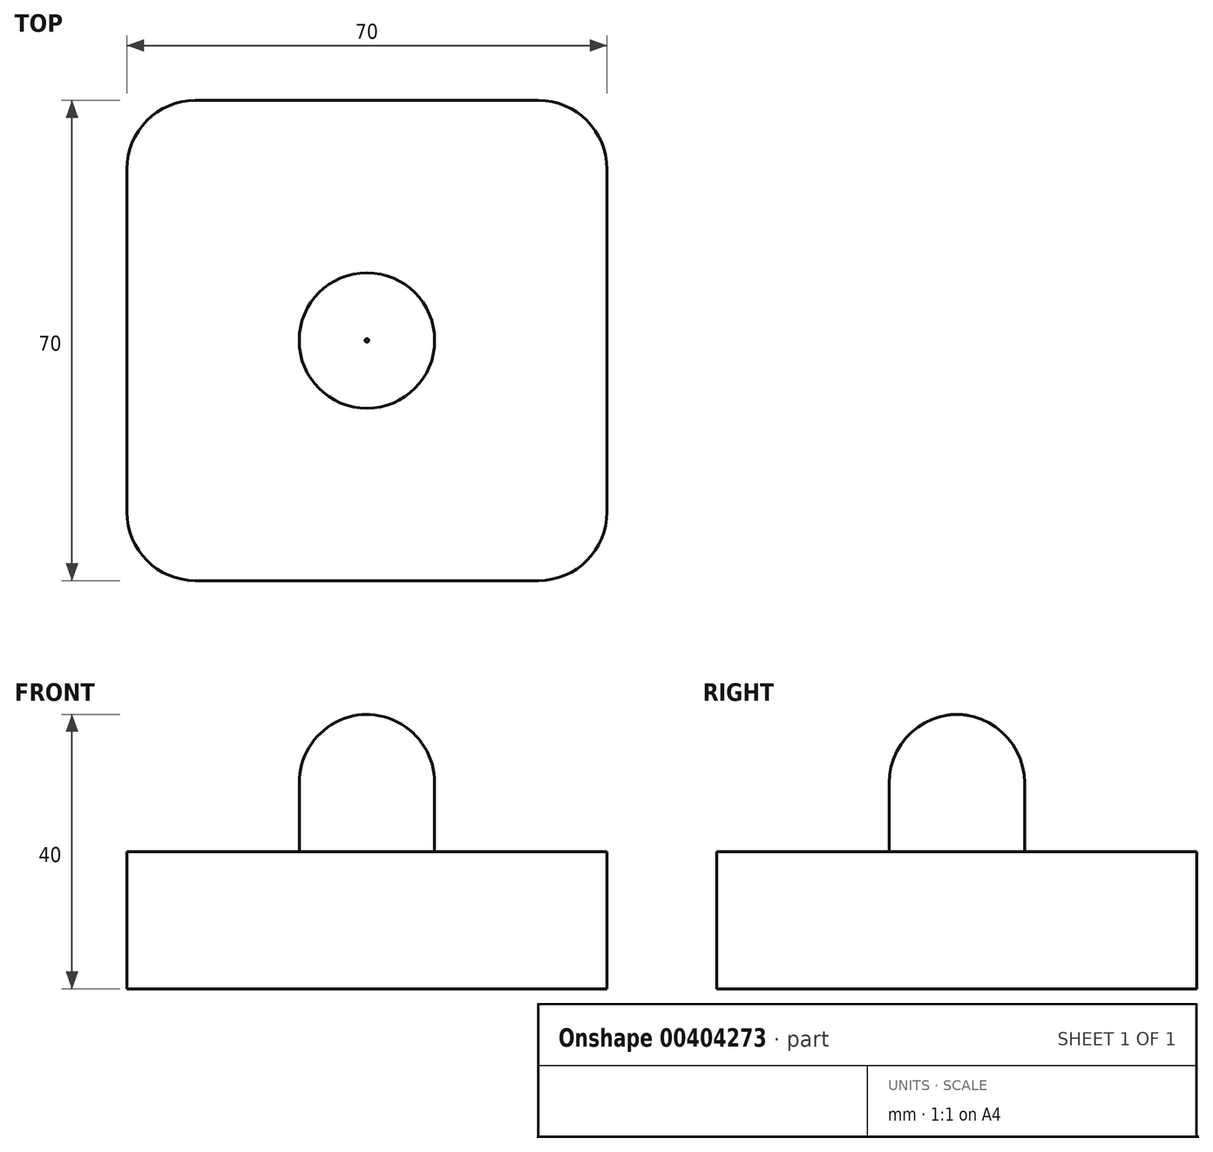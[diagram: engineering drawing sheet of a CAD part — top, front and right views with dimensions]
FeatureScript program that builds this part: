
annotation { "Feature Type Name" : "Feature", "Feature Type Description" : "" }
export const myFeature = defineFeature(function(context is Context, id is Id, definition is map)
    precondition{}
    {
        {
            var Q0;
            Q0=qCreatedBy(makeId("Top.planeOp"),FACE);
            var sketch = newSketch(context, id + "F0", { "sketchPlane" : qUnion([Q0])});
            skLineSegment(sketch, "E0.bottom", {"start": v(35, -35) * mm, "end": v(-35, -35) * mm});
            skLineSegment(sketch, "E0.top", {"start": v(35, 35) * mm, "end": v(-35, 35) * mm});
            skLineSegment(sketch, "E0.left", {"start": v(35, -35) * mm, "end": v(35, 35) * mm});
            skLineSegment(sketch, "E0.right", {"start": v(-35, -35) * mm, "end": v(-35, 35) * mm});
            skPoint(sketch, "E0.middle", {"position": v(0, 0) * mm});
            skSolve(sketch);
        }
        {
            var Q0;
            Q0=makeQuery(id+"F0.imprint","IMPRINT",FACE,{"disambiguationData":[TD([[makeQuery(id+"F0.imprint","IMPRINT",EDGE,{"derivedFrom":sQuery(id+"F0.wireOp",EDGE,"E0.bottom")}),-1.0]])]});
            extrude(context, id + "F1", {"entities" : qUnion([Q0]), "oppositeDirection" : true, "depth" : 20 * mm});
        }
        {
            var Q0;
            Q0=qCreatedBy(makeId("Front.planeOp"),FACE);
            var sketch = newSketch(context, id + "F2", { "sketchPlane" : qUnion([Q0])});
            skLineSegment(sketch, "E1", {"start": v(0, 0) * mm, "end": v(0, 20) * mm});
            skArc(sketch, "E2", {"start": v(0, 0) * mm, "mid": v(9.87, 10) * mm, "end": v(0, 20) * mm});
            skLineSegment(sketch, "E3", {"start": v(9.87, 10) * mm, "end": v(9.87, 0) * mm});
            skLineSegment(sketch, "E4", {"start": v(9.87, 0) * mm, "end": v(0, 0) * mm});
            skSolve(sketch);
        }
        {
            var Q0;
            {var subQ0=sQuery(id+"F2.wireOp",EDGE,"E1");Q0=makeQuery(id+"F2.imprint","IMPRINT",FACE,{"disambiguationData":[TD([[makeQuery(id+"F2.imprint","IMPRINT",EDGE,{"derivedFrom":subQ0}),-1.0]])]});}
            var Q1;
            {var subQ2=sQuery(id+"F2.wireOp",EDGE,"E3");Q1=makeQuery(id+"F2.imprint","IMPRINT",FACE,{"disambiguationData":[TD([[makeQuery(id+"F2.imprint","IMPRINT",EDGE,{"derivedFrom":subQ2}),-1.0]])]});}
            var Q2;
            Q2=sQuery(id+"F2.wireOp",EDGE,"E1");
            revolve(context, id + "F3", {"operationType" : NewBodyOperationType.ADD, "entities" : qUnion([Q0, Q1]), "axis" : qUnion([Q2]), "revolveType" : RevolveType.FULL});
        }
        {
            var Q0;
            Q0=makeQuery(id+"F1.opExtrude","SWEPT_EDGE",EDGE,{"disambiguationData":[OSD([sQuery(id+"F0.wireOp",EDGE,"E0.bottom"),sQuery(id+"F0.wireOp",EDGE,"E0.left")])]});
            var Q1;
            Q1=makeQuery(id+"F1.opExtrude","SWEPT_EDGE",EDGE,{"disambiguationData":[OSD([sQuery(id+"F0.wireOp",EDGE,"E0.bottom"),sQuery(id+"F0.wireOp",EDGE,"E0.right")])]});
            var Q2;
            Q2=makeQuery(id+"F1.opExtrude","SWEPT_EDGE",EDGE,{"disambiguationData":[OSD([sQuery(id+"F0.wireOp",EDGE,"E0.top"),sQuery(id+"F0.wireOp",EDGE,"E0.left")])]});
            var Q3;
            Q3=makeQuery(id+"F1.opExtrude","SWEPT_EDGE",EDGE,{"disambiguationData":[OSD([sQuery(id+"F0.wireOp",EDGE,"E0.top"),sQuery(id+"F0.wireOp",EDGE,"E0.right")])]});
            fillet(context, id + "F4", {"entities" : qUnion([Q0, Q1, Q2, Q3]), "radius" : 10 * mm, "tangentPropagation" : true, "allowEdgeOverflow" : false});
        }
    });
